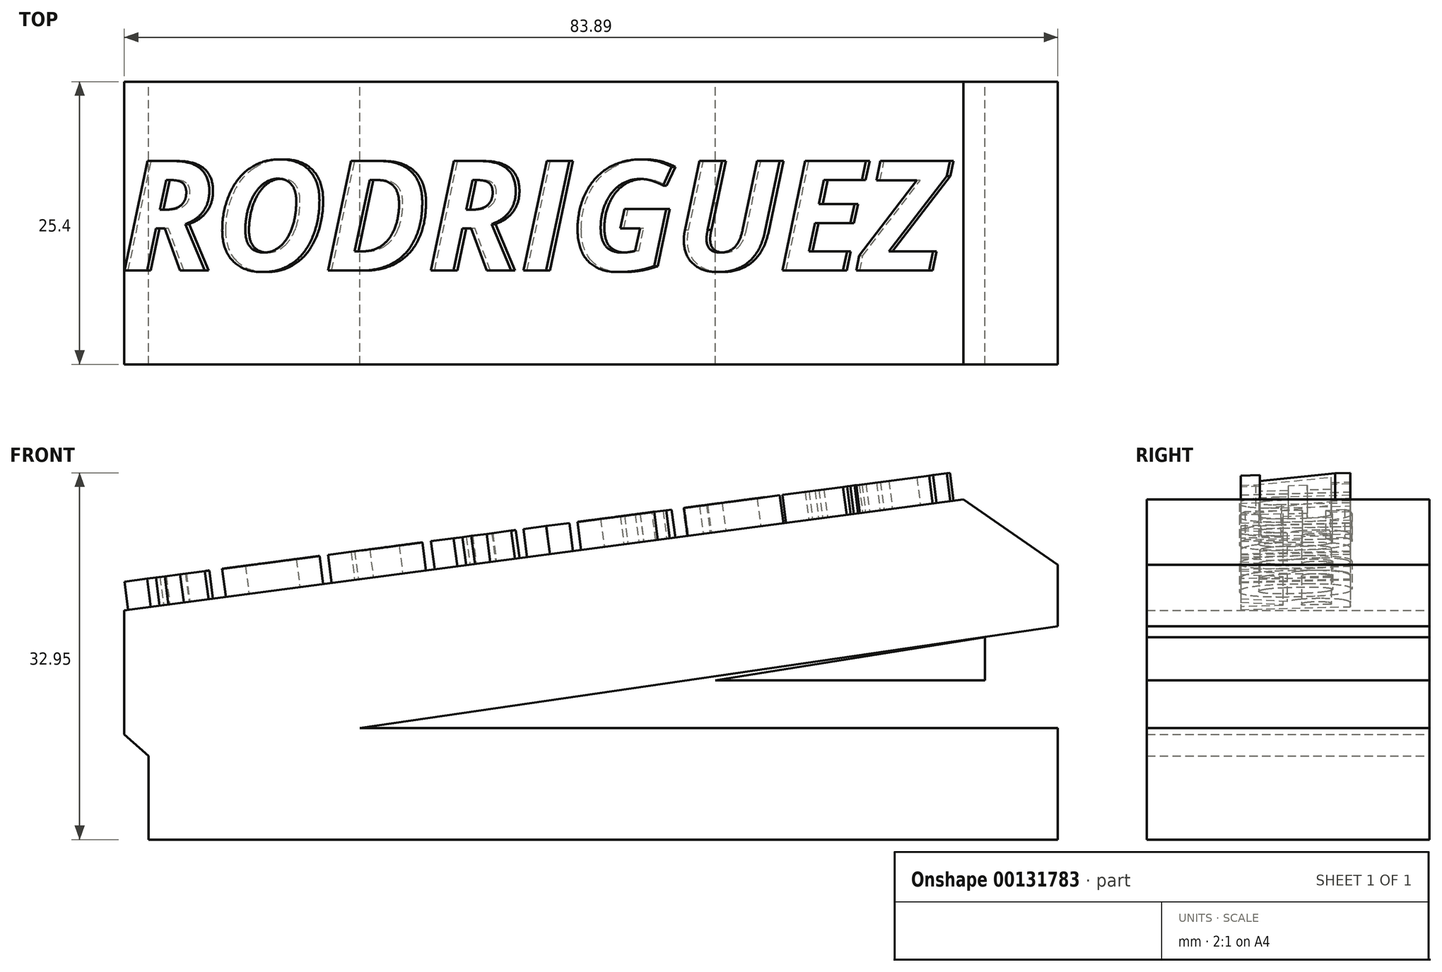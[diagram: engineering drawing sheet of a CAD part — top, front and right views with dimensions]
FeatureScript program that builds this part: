
annotation { "Feature Type Name" : "Feature", "Feature Type Description" : "" }
export const myFeature = defineFeature(function(context is Context, id is Id, definition is map)
    precondition{}
    {
        {
            var Q0;
            Q0=qCreatedBy(makeId("Front.planeOp"),FACE);
            var sketch = newSketch(context, id + "F0", { "sketchPlane" : qUnion([Q0])});
            skLineSegment(sketch, "E0", {"start": v(-50.92, 0) * mm, "end": v(30.8, 0) * mm});
            skLineSegment(sketch, "E1", {"start": v(30.8, 0) * mm, "end": v(30.8, 4.12) * mm});
            skLineSegment(sketch, "E2", {"start": v(-50.92, 0) * mm, "end": v(-50.92, 4.12) * mm});
            skLineSegment(sketch, "E3", {"start": v(-50.92, 4.12) * mm, "end": v(-50.92, 7.52) * mm});
            skLineSegment(sketch, "E4", {"start": v(-50.92, 7.52) * mm, "end": v(-53.1, 9.46) * mm});
            skLineSegment(sketch, "E5", {"start": v(-53.1, 9.46) * mm, "end": v(-53.1, 20.6) * mm});
            skLineSegment(sketch, "E6", {"start": v(-53.1, 20.6) * mm, "end": v(22.3, 30.55) * mm});
            skLineSegment(sketch, "E7", {"start": v(22.3, 30.55) * mm, "end": v(30.8, 24.67) * mm});
            skLineSegment(sketch, "E8", {"start": v(30.8, 24.67) * mm, "end": v(30.8, 19.15) * mm});
            skLineSegment(sketch, "E9", {"start": v(-31.93, 10.03) * mm, "end": v(30.8, 10.03) * mm});
            skLineSegment(sketch, "E10", {"start": v(30.8, 10.03) * mm, "end": v(30.8, 0) * mm});
            skLineSegment(sketch, "E11", {"start": v(-31.93, 10.03) * mm, "end": v(30.8, 19.15) * mm});
            skSolve(sketch);
        }
        {
            var Q0;
            Q0=qCreatedBy(makeId("Front.planeOp"),FACE);
            var sketch = newSketch(context, id + "F1", { "sketchPlane" : qUnion([Q0])});
            skLineSegment(sketch, "E12", {"start": v(24.25, 18.18) * mm, "end": v(24.25, 14.3) * mm});
            skLineSegment(sketch, "E13", {"start": v(24.25, 14.3) * mm, "end": v(0, 14.3) * mm});
            skLineSegment(sketch, "E14", {"start": v(24.25, 18.18) * mm, "end": v(0, 14.3) * mm});
            skSolve(sketch);
        }
        {
            var Q0;
            Q0 = qSketchRegion(id + "F0", true);
            extrude(context, id + "F2", {"entities" : qUnion([Q0]), "depth" : 25.4 * mm});
        }
        {
            var Q0;
            Q0 = qSketchRegion(id + "F1", true);
            extrude(context, id + "F3", {"entities" : qUnion([Q0]), "depth" : 25.4 * mm});
        }
        {
            var Q0;
            Q0=makeQuery(id+"F2.opExtrude","SWEPT_FACE",FACE,{"disambiguationData":[OSD([sQuery(id+"F0.wireOp",EDGE,"E6")])]});
            var sketch = newSketch(context, id + "F4", { "sketchPlane" : qUnion([Q0])});
            skText(sketch, "E15", { "text": "RODRIGUEZ", "fontName": "OpenSans-BoldItalic.ttf"});
            const initialGuessF4  = {"E15": [-0.04995, -0.01697, 1, 0, 0.00992]};
            skSetInitialGuess(sketch, initialGuessF4);
            skSolve(sketch);
        }
        {
            var Q0;
            Q0 = qSketchRegion(id + "F4", true);
            extrude(context, id + "F5", {"entities" : qUnion([Q0]), "operationType" : NewBodyOperationType.ADD, "depth" : 2.54 * mm});
        }
    });
